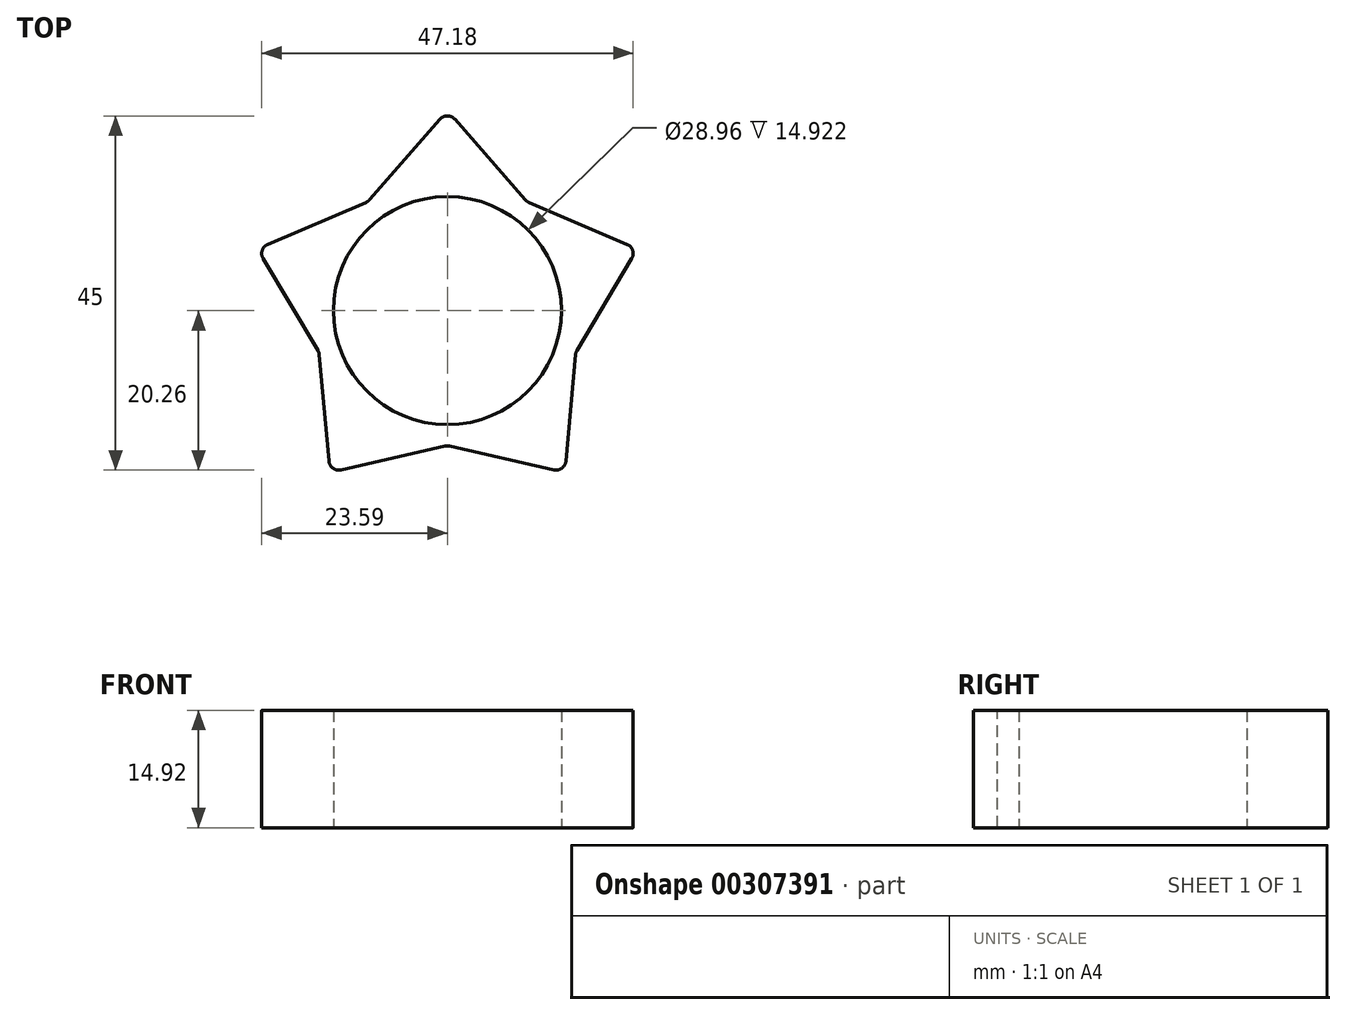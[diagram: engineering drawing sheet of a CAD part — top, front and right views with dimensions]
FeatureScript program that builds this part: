
annotation { "Feature Type Name" : "Feature", "Feature Type Description" : "" }
export const myFeature = defineFeature(function(context is Context, id is Id, definition is map)
    precondition{}
    {
        {
            var Q0;
            Q0=qCreatedBy(makeId("Top.planeOp"),FACE);
            var sketch = newSketch(context, id + "F0", { "sketchPlane" : qUnion([Q0])});
            skCircle(sketch, "E0", {"center": v(0, 0) * mm, "radius": 16.51 * mm, "construction": true});
            skCircle(sketch, "E1", {"center": v(0, 0) * mm, "radius": 14.48 * mm});
            skPoint(sketch, "E2", {"position": v(0, 25.4) * mm});
            skPoint(sketch, "E3.1.0", {"position": v(-24.16, 7.85) * mm});
            skPoint(sketch, "E3.2.0", {"position": v(-14.93, -20.55) * mm});
            skPoint(sketch, "E3.3.0", {"position": v(14.93, -20.55) * mm});
            skPoint(sketch, "E3.4.0", {"position": v(24.16, 7.85) * mm});
            skLineSegment(sketch, "E4", {"start": v(0, 25.4) * mm, "end": v(10.08, 13.87) * mm});
            skLineSegment(sketch, "E5", {"start": v(10.08, 13.87) * mm, "end": v(24.16, 7.85) * mm});
            skLineSegment(sketch, "E6", {"start": v(24.16, 7.85) * mm, "end": v(16.3, -5.3) * mm});
            skLineSegment(sketch, "E7", {"start": v(16.3, -5.3) * mm, "end": v(14.93, -20.55) * mm});
            skLineSegment(sketch, "E8", {"start": v(0, -17.14) * mm, "end": v(-14.93, -20.55) * mm});
            skLineSegment(sketch, "E9", {"start": v(-16.3, -5.3) * mm, "end": v(-14.93, -20.55) * mm});
            skLineSegment(sketch, "E10", {"start": v(-16.3, -5.3) * mm, "end": v(-24.16, 7.85) * mm});
            skLineSegment(sketch, "E11", {"start": v(-24.16, 7.85) * mm, "end": v(-10.08, 13.87) * mm});
            skLineSegment(sketch, "E12", {"start": v(-10.08, 13.87) * mm, "end": v(0, 25.4) * mm});
            skLineSegment(sketch, "E13", {"start": v(14.93, -20.55) * mm, "end": v(0, -17.15) * mm});
            skCircle(sketch, "E14", {"center": v(0, 0) * mm, "radius": 17.15 * mm, "construction": true});
            skSolve(sketch);
        }
        {
            var Q0;
            Q0=makeQuery(id+"F0.imprint","IMPRINT",FACE,{"disambiguationData":[TD([[makeQuery(id+"F0.imprint","IMPRINT",EDGE,{"derivedFrom":sQuery(id+"F0.wireOp",EDGE,"E1")}),-1.0]])]});
            extrude(context, id + "F1", {"entities" : qUnion([Q0]), "depth" : 14.92 * mm});
        }
        {
            var Q0;
            Q0=makeQuery(id+"F1.opExtrude","SWEPT_EDGE",EDGE,{"disambiguationData":[OSD([sQuery(id+"F0.wireOp",EDGE,"E8"),sQuery(id+"F0.wireOp",EDGE,"E9")])]});
            var Q1;
            Q1=makeQuery(id+"F1.opExtrude","SWEPT_EDGE",EDGE,{"disambiguationData":[OSD([sQuery(id+"F0.wireOp",EDGE,"E7"),sQuery(id+"F0.wireOp",EDGE,"E13")])]});
            var Q2;
            Q2=makeQuery(id+"F1.opExtrude","SWEPT_EDGE",EDGE,{"disambiguationData":[OSD([sQuery(id+"F0.wireOp",EDGE,"E10"),sQuery(id+"F0.wireOp",EDGE,"E11")])]});
            var Q3;
            Q3=makeQuery(id+"F1.opExtrude","SWEPT_EDGE",EDGE,{"disambiguationData":[OSD([sQuery(id+"F0.wireOp",EDGE,"E5"),sQuery(id+"F0.wireOp",EDGE,"E6")])]});
            var Q4;
            Q4=makeQuery(id+"F1.opExtrude","SWEPT_EDGE",EDGE,{"disambiguationData":[OSD([sQuery(id+"F0.wireOp",EDGE,"E4"),sQuery(id+"F0.wireOp",EDGE,"E12")])]});
            var Q5;
            Q5=makeQuery(id+"F1.opExtrude","SWEPT_EDGE",EDGE,{"disambiguationData":[OSD([sQuery(id+"F0.wireOp",EDGE,"E9"),sQuery(id+"F0.wireOp",EDGE,"E10")])]});
            var Q6;
            Q6=makeQuery(id+"F1.opExtrude","SWEPT_EDGE",EDGE,{"disambiguationData":[OSD([sQuery(id+"F0.wireOp",EDGE,"E8"),sQuery(id+"F0.wireOp",EDGE,"E13")])]});
            var Q7;
            Q7=makeQuery(id+"F1.opExtrude","SWEPT_EDGE",EDGE,{"disambiguationData":[OSD([sQuery(id+"F0.wireOp",EDGE,"E6"),sQuery(id+"F0.wireOp",EDGE,"E7")])]});
            var Q8;
            Q8=makeQuery(id+"F1.opExtrude","SWEPT_EDGE",EDGE,{"disambiguationData":[OSD([sQuery(id+"F0.wireOp",EDGE,"E4"),sQuery(id+"F0.wireOp",EDGE,"E5")])]});
            var Q9;
            Q9=makeQuery(id+"F1.opExtrude","SWEPT_EDGE",EDGE,{"disambiguationData":[OSD([sQuery(id+"F0.wireOp",EDGE,"E11"),sQuery(id+"F0.wireOp",EDGE,"E12")])]});
            fillet(context, id + "F2", {"entities" : qUnion([Q0, Q1, Q2, Q3, Q4, Q5, Q6, Q7, Q8, Q9]), "radius" : 1.27 * mm, "tangentPropagation" : true, "allowEdgeOverflow" : false});
        }
    });
